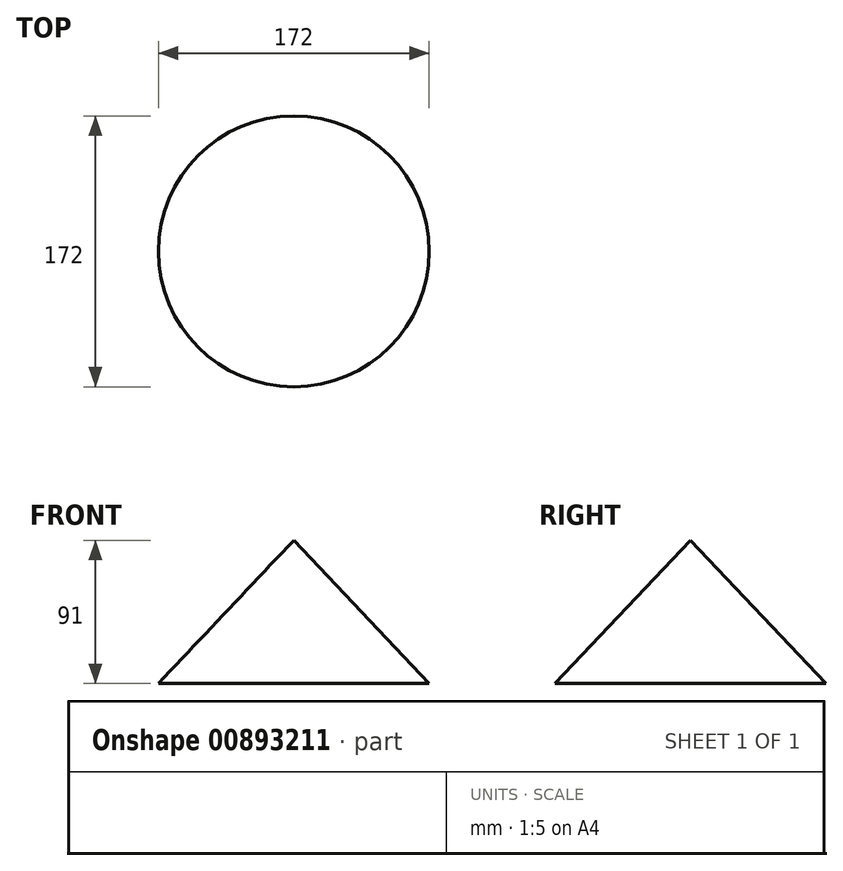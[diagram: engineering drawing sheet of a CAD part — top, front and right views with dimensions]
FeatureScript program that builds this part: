
annotation { "Feature Type Name" : "Feature", "Feature Type Description" : "" }
export const myFeature = defineFeature(function(context is Context, id is Id, definition is map)
    precondition{}
    {
        {
            var Q0;
            Q0=qCreatedBy(makeId("Front.planeOp"),FACE);
            var sketch = newSketch(context, id + "F0", { "sketchPlane" : qUnion([Q0])});
            skLineSegment(sketch, "E0", {"start": v(0, 0) * mm, "end": v(0, 91) * mm});
            skLineSegment(sketch, "E1", {"start": v(0, 91) * mm, "end": v(-86, 0) * mm});
            skLineSegment(sketch, "E2", {"start": v(-86, 0) * mm, "end": v(0, 0) * mm});
            skSolve(sketch);
        }
        {
            var Q0;
            Q0=qCreatedBy(makeId("Top.planeOp"),FACE);
            var sketch = newSketch(context, id + "F1", { "sketchPlane" : qUnion([Q0])});
            skCircle(sketch, "E3", {"center": v(0, 0) * mm, "radius": 86 * mm});
            skSolve(sketch);
        }
        {
            var Q0;
            Q0=makeQuery(id+"F1.imprint","IMPRINT",FACE,{"disambiguationData":[TD([[makeQuery(id+"F1.imprint","IMPRINT",EDGE,{"derivedFrom":sQuery(id+"F1.wireOp",EDGE,"E3")}),1.0]])]});
            var Q1;
            Q1=sQuery(id+"F0.wireOp",VERTEX,"E0.end");
            var Q2;
            Q2=sQuery(id+"F1.wireOp",EDGE,"E3");
            var Q3;
            Q3=sQuery(id+"F0.wireOp",VERTEX,"E0.end");
            loft(context, id + "F2", {"bodyType" : ToolBodyType.SURFACE, "sheetProfilesArray" : [{ "sheetProfileEntities" : qUnion([Q0]) }, { "sheetProfileEntities" : qUnion([Q1]) }], "wireProfilesArray" : [{ "wireProfileEntities" : qUnion([Q2]) }, { "wireProfileEntities" : qUnion([Q3]) }]});
        }
    });
